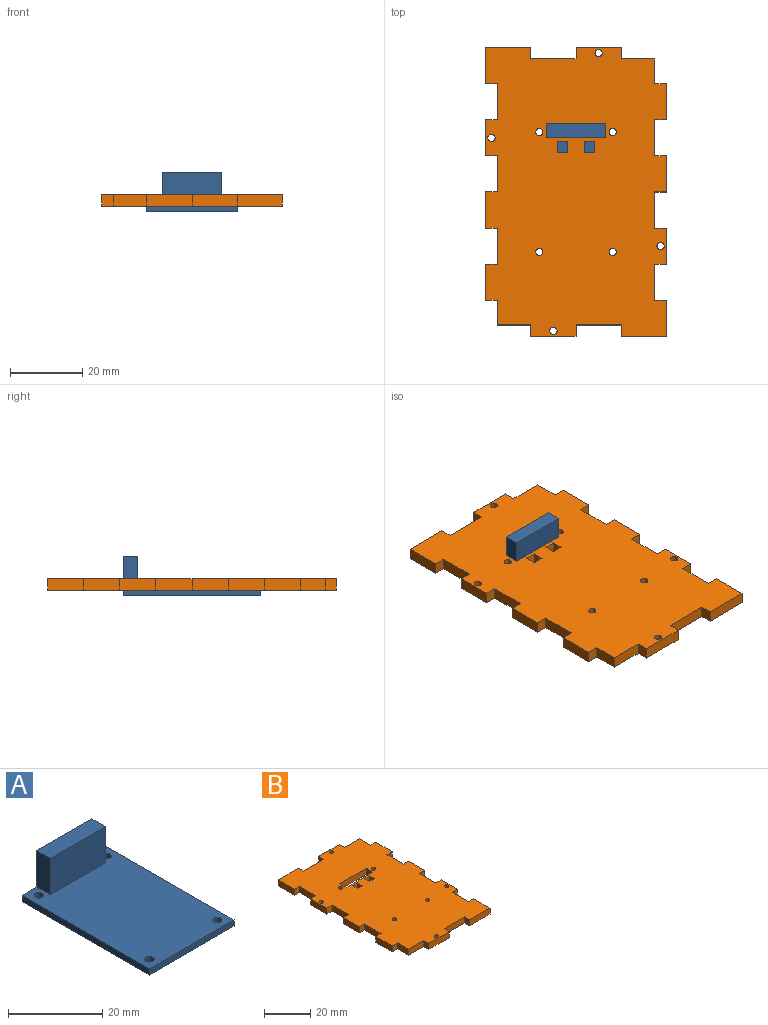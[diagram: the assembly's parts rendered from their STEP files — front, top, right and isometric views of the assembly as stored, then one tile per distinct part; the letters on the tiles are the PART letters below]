
ASSEMBLY  parts=2 mates=1
PART A: 14 faces, bbox 25.4x38.1x11 mm
  f0: plane 38.1x25.4mm, normal (0,0,1), area 889.2mm2, adj f1,f2,f3,f4,f5,f6,f7,f8
  f1: plane 38.1x1.6mm, normal (1,0,0), area 61mm2, adj f0,f2,f7,f9
  f2: plane 25.4x11mm, normal (0,1,0), area 195.7mm2, adj f0,f1,f3,f9,f10,f11,f13
  f3: plane 38.1x1.6mm, normal (-1,0,0), area 61mm2, adj f0,f2,f7,f9
  f4: cylinder r=1mm len=2mm, axis (0,0,-1), area 10.1mm2, adj f0,f9
  f5: cylinder r=1mm len=2mm, axis (0,0,-1), area 10.1mm2, adj f0,f9
  f6: cylinder r=1mm len=2mm, axis (0,0,-1), area 10.1mm2, adj f0,f9
  f7: plane 25.4x1.6mm, normal (0,-1,0), area 40.6mm2, adj f0,f1,f3,f9
  f8: cylinder r=1mm len=2mm, axis (0,0,-1), area 10.1mm2, adj f0,f9
  f9: plane 38.1x25.4mm, normal (0,0,-1), area 955.2mm2, adj f1,f2,f3,f4,f5,f6,f7,f8
  f10: plane 9.4x4mm, normal (1,0,0), area 37.6mm2, adj f0,f2,f12,f13
  f11: plane 9.4x4mm, normal (-1,0,0), area 37.6mm2, adj f0,f2,f12,f13
  f12: plane 16.5x9.4mm, normal (0,-1,0), area 155.1mm2, adj f0,f10,f11,f13
  f13: plane 16.5x4mm, normal (0,0,1), area 66mm2, adj f2,f10,f11,f12
PART B: 66 faces, bbox 50x80x3.2 mm
  f0: plane 80x50mm, normal (0,0,1), area 3498.3mm2, adj f2,f3,f4,f5,f6,f7,f8,f9
  f1: plane 80x50mm, normal (0,0,-1), area 3498.3mm2, adj f2,f3,f4,f5,f6,f7,f8,f9
  f2: plane 3.18x3.18mm, normal (0,-1,0), area 10.1mm2, adj f0,f1,f3,f48
  f3: plane 10x3.18mm, normal (-1,0,0), area 31.7mm2, adj f0,f1,f2,f4
  f4: plane 3.18x3.18mm, normal (0,1,0), area 10.1mm2, adj f0,f1,f3,f5
  f5: plane 10x3.18mm, normal (-1,0,0), area 31.8mm2, adj f0,f1,f4,f6
  f6: plane 3.18x3.18mm, normal (0,-1,0), area 10.1mm2, adj f0,f1,f5,f7
  f7: plane 10x3.18mm, normal (-1,0,0), area 31.8mm2, adj f0,f1,f6,f8
  f8: plane 3.18x3.18mm, normal (0,1,0), area 10.1mm2, adj f0,f1,f7,f9
  f9: plane 10x3.18mm, normal (-1,0,0), area 31.8mm2, adj f0,f1,f8,f10
  f10: plane 3.18x3.18mm, normal (0,-1,0), area 10.1mm2, adj f0,f1,f9,f11
  f11: plane 10x3.18mm, normal (-1,0,0), area 31.8mm2, adj f0,f1,f10,f12
  f12: plane 3.18x3.18mm, normal (0,1,0), area 10.1mm2, adj f0,f1,f11,f13
  f13: plane 10x3.18mm, normal (-1,0,0), area 31.7mm2, adj f0,f1,f12,f14
  f14: plane 3.18x3.18mm, normal (0,-1,0), area 10.1mm2, adj f0,f1,f13,f15
  f15: plane 6.83x3.18mm, normal (-1,0,0), area 21.7mm2, adj f0,f1,f14,f16
  f16: plane 9.33x3.18mm, normal (0,-1,0), area 29.6mm2, adj f0,f1,f15,f17
  f17: plane 3.18x3.18mm, normal (-1,0,0), area 10.1mm2, adj f0,f1,f16,f18
  f18: plane 12.5x3.18mm, normal (0,-1,0), area 39.7mm2, adj f0,f1,f17,f19
  f19: plane 3.18x3.18mm, normal (1,0,0), area 10.1mm2, adj f0,f1,f18,f20
  f20: plane 12.5x3.18mm, normal (0,-1,0), area 39.7mm2, adj f0,f1,f19,f21
  f21: plane 3.18x3.18mm, normal (-1,0,0), area 10.1mm2, adj f0,f1,f20,f22
  f22: plane 12.5x3.18mm, normal (0,-1,0), area 39.7mm2, adj f0,f1,f21,f23
  f23: plane 10x3.18mm, normal (1,0,0), area 31.8mm2, adj f0,f1,f22,f24
  f24: plane 3.18x3.18mm, normal (0,1,0), area 10.1mm2, adj f0,f1,f23,f25
  f25: plane 10x3.18mm, normal (1,0,0), area 31.7mm2, adj f0,f1,f24,f26
  f26: plane 3.18x3.18mm, normal (0,-1,0), area 10.1mm2, adj f0,f1,f25,f27
  f27: plane 10x3.18mm, normal (1,0,0), area 31.8mm2, adj f0,f1,f26,f28
  f28: plane 3.18x3.18mm, normal (0,1,0), area 10.1mm2, adj f0,f1,f27,f29
  f29: plane 10x3.18mm, normal (1,0,0), area 31.8mm2, adj f0,f1,f28,f30
  f30: plane 3.18x3.18mm, normal (0,-1,0), area 10.1mm2, adj f0,f1,f29,f31
  f31: plane 10x3.18mm, normal (1,0,0), area 31.8mm2, adj f0,f1,f30,f32
  f32: plane 3.18x3.18mm, normal (0,1,0), area 10.1mm2, adj f0,f1,f31,f33
  f33: plane 10x3.18mm, normal (1,0,0), area 31.8mm2, adj f0,f1,f32,f34
  f34: plane 3.18x3.18mm, normal (0,-1,0), area 10.1mm2, adj f0,f1,f33,f35
  f35: plane 10x3.18mm, normal (1,0,0), area 31.7mm2, adj f0,f1,f34,f36
  f36: plane 3.18x3.18mm, normal (0,1,0), area 10.1mm2, adj f0,f1,f35,f37
  f37: plane 6.83x3.18mm, normal (1,0,0), area 21.7mm2, adj f0,f1,f36,f38
  f38: plane 9.33x3.18mm, normal (0,1,0), area 29.6mm2, adj f0,f1,f37,f39
  f39: plane 3.18x3.18mm, normal (1,0,0), area 10.1mm2, adj f0,f1,f38,f40
  f40: plane 12.5x3.18mm, normal (0,1,0), area 39.7mm2, adj f0,f1,f39,f41
  f41: plane 3.18x3.18mm, normal (-1,0,0), area 10.1mm2, adj f0,f1,f40,f42
  f42: plane 12.5x3.18mm, normal (0,1,0), area 39.7mm2, adj f0,f1,f41,f43
  f43: plane 3.18x3.18mm, normal (1,0,0), area 10.1mm2, adj f0,f1,f42,f44
  f44: plane 12.5x3.18mm, normal (0,1,0), area 39.7mm2, adj f0,f1,f43,f48
  f45: cylinder r=1mm len=3.18mm, axis (0,0,-1), area 19.9mm2, adj f0,f1
  f46: cylinder r=1mm len=3.18mm, axis (0,0,-1), area 19.9mm2, adj f0,f1
  f47: cylinder r=1mm len=3.18mm, axis (0,0,-1), area 19.9mm2, adj f0,f1
  f48: plane 10x3.18mm, normal (-1,0,0), area 31.8mm2, adj f0,f1,f2,f44
  f49: cylinder r=1mm len=3.18mm, axis (0,0,-1), area 19.9mm2, adj f0,f1
  f50: cylinder r=1mm len=3.18mm, axis (0,0,1), area 19.9mm2, adj f0,f1
  f51: plane 4x3.18mm, normal (-1,0,0), area 12.7mm2, adj f0,f1,f52,f54
  f52: plane 16.5x3.18mm, normal (0,-1,0), area 52.4mm2, adj f0,f1,f51,f53
  f53: plane 4x3.18mm, normal (1,0,0), area 12.7mm2, adj f0,f1,f52,f54
  f54: plane 16.5x3.18mm, normal (0,1,0), area 52.4mm2, adj f0,f1,f51,f53
  f55: cylinder r=1mm len=3.18mm, axis (0,0,1), area 19.9mm2, adj f0,f1
  f56: cylinder r=1mm len=3.18mm, axis (0,0,1), area 19.9mm2, adj f0,f1
  f57: cylinder r=1mm len=3.18mm, axis (0,0,1), area 19.9mm2, adj f0,f1
  f58: plane 3.18x3mm, normal (0,-1,0), area 9.5mm2, adj f0,f1,f59,f61
  f59: plane 3.18x3mm, normal (1,0,0), area 9.5mm2, adj f0,f1,f58,f60
  f60: plane 3.18x3mm, normal (0,1,0), area 9.5mm2, adj f0,f1,f59,f61
  f61: plane 3.18x3mm, normal (-1,0,0), area 9.5mm2, adj f0,f1,f58,f60
  f62: plane 3.18x3mm, normal (-1,0,0), area 9.5mm2, adj f0,f1,f63,f65
  f63: plane 3.18x3mm, normal (0,-1,0), area 9.5mm2, adj f0,f1,f62,f64
  f64: plane 3.18x3mm, normal (1,0,0), area 9.5mm2, adj f0,f1,f63,f65
  f65: plane 3.18x3mm, normal (0,1,0), area 9.5mm2, adj f0,f1,f62,f64
PLACE A t=(-4.8,-1.96,-1.97)mm
PLACE B t=(-4.8,-1.96,-0.37)mm
MATE fastened A.f0 <-> B.f1  axis (0,0,1) through (-4.8,-1.96,-0.37)mm
